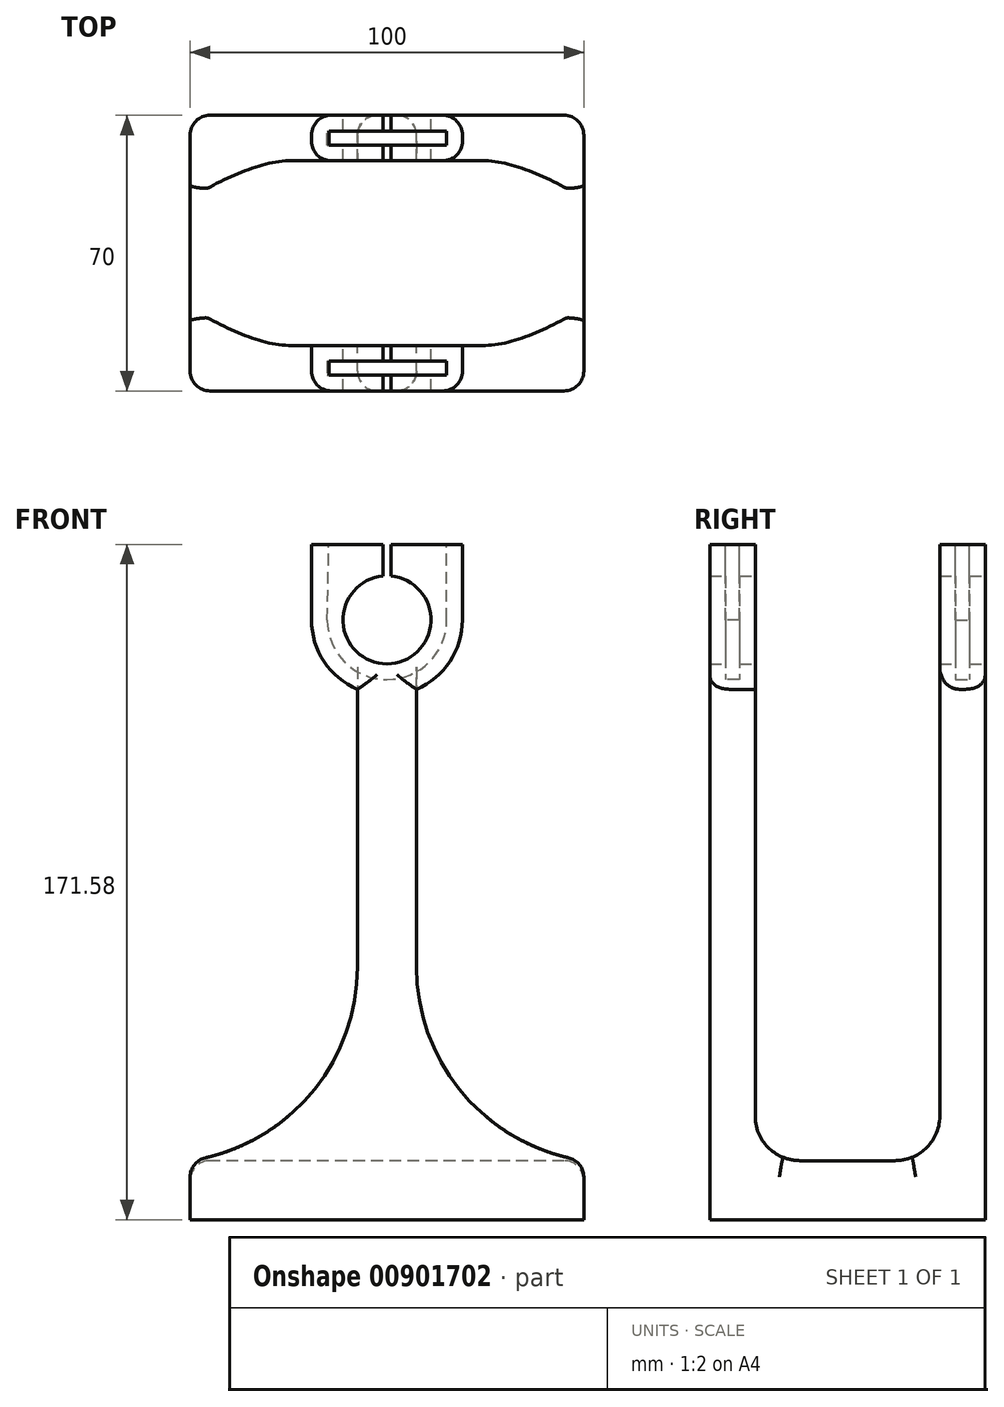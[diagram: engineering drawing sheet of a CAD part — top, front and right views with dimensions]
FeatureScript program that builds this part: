
annotation { "Feature Type Name" : "Feature", "Feature Type Description" : "" }
export const myFeature = defineFeature(function(context is Context, id is Id, definition is map)
    precondition{}
    {
        {
            var Q0;
            Q0=qCreatedBy(makeId("Front.planeOp"),FACE);
            var sketch = newSketch(context, id + "F0", { "sketchPlane" : qUnion([Q0])});
            skPoint(sketch, "E0.middle", {"position": v(0, 0) * mm});
            skArc(sketch, "E1", {"start": v(-15.18, 20.78) * mm, "mid": v(-13.12, 13.15) * mm, "end": v(-7.5, 7.59) * mm});
            skLineSegment(sketch, "E2.top", {"start": v(-19.18, 39.96) * mm, "end": v(19.17, 39.96) * mm});
            skLineSegment(sketch, "E2.left", {"start": v(-19.17, 20.78) * mm, "end": v(-19.17, 39.96) * mm});
            skLineSegment(sketch, "E2.right", {"start": v(19.17, 20.78) * mm, "end": v(19.17, 39.96) * mm});
            skArc(sketch, "E3", {"start": v(-19.17, 20.78) * mm, "mid": v(-16, 10.2) * mm, "end": v(-7.5, 3.13) * mm});
            skLineSegment(sketch, "E4", {"start": v(-15.18, 20.78) * mm, "end": v(-14.78, 39.96) * mm});
            skLineSegment(sketch, "E5", {"start": v(15.18, 20.78) * mm, "end": v(15.18, 39.96) * mm});
            skLineSegment(sketch, "E6.top", {"start": v(-7.5, -131.62) * mm, "end": v(7.5, -131.62) * mm});
            skLineSegment(sketch, "E7.bottom", {"start": v(-50, -131.62) * mm, "end": v(50, -131.62) * mm});
            skLineSegment(sketch, "E7.top", {"start": v(-50, -116.62) * mm, "end": v(-7.5, -116.62) * mm});
            skLineSegment(sketch, "E7.left", {"start": v(-50, -131.62) * mm, "end": v(-50, -116.62) * mm});
            skLineSegment(sketch, "E7.right", {"start": v(50, -131.62) * mm, "end": v(50, -116.62) * mm});
            skLineSegment(sketch, "E8", {"start": v(7.5, -116.62) * mm, "end": v(50, -116.62) * mm});
            skArc(sketch, "E9", {"start": v(7.5, 3.13) * mm, "mid": v(16, 10.2) * mm, "end": v(19.17, 20.78) * mm});
            skLineSegment(sketch, "E10", {"start": v(-7.5, 3.13) * mm, "end": v(-7.5, -116.62) * mm});
            skLineSegment(sketch, "E11", {"start": v(-7.5, 7.59) * mm, "end": v(-7.5, 7.59) * mm});
            skArc(sketch, "E12", {"start": v(7.5, 7.59) * mm, "mid": v(13.12, 13.15) * mm, "end": v(15.18, 20.78) * mm});
            skArc(sketch, "E13", {"start": v(-7.5, 7.59) * mm, "mid": v(0, 5.6) * mm, "end": v(7.5, 7.59) * mm});
            skLineSegment(sketch, "E14", {"start": v(7.5, 3.13) * mm, "end": v(7.5, -116.62) * mm});
            skPoint(sketch, "E15", {"position": v(0, 5.6) * mm});
            skCircle(sketch, "E16", {"center": v(0, 20.78) * mm, "radius": 11.18 * mm});
            skLineSegment(sketch, "E17.bottom", {"start": v(1, 20.78) * mm, "end": v(-1, 20.78) * mm});
            skLineSegment(sketch, "E17.top", {"start": v(1, 39.96) * mm, "end": v(-1, 39.96) * mm});
            skLineSegment(sketch, "E17.left", {"start": v(1, 20.78) * mm, "end": v(1, 39.96) * mm});
            skLineSegment(sketch, "E17.right", {"start": v(-1, 20.78) * mm, "end": v(-1, 39.96) * mm});
            skSolve(sketch);
        }
        {
            var Q0;
            Q0=makeQuery(id+"F0.imprint","IMPRINT",FACE,{"disambiguationData":[TD([[makeQuery(id+"F0.imprint","IMPRINT",EDGE,{"derivedFrom":sQuery(id+"F0.wireOp",EDGE,"E1")}),-1.0]])]});
            var Q1;
            Q1=makeQuery(id+"F0.imprint","IMPRINT",FACE,{"disambiguationData":[TD([[makeQuery(id+"F0.imprint","IMPRINT",EDGE,{"derivedFrom":sQuery(id+"F0.wireOp",EDGE,"E1")}),1.0]])]});
            extrude(context, id + "F1", {"entities" : qUnion([Q0, Q1]), "depth" : 70 * mm, "offsetDistance" : 25 * mm});
        }
        {
            var Q0;
            Q0=makeQuery(id+"F1.opExtrude","SWEPT_FACE",FACE,{"disambiguationData":[OSD([sQuery(id+"F0.wireOp",EDGE,"E2.top")])]});
            var Q1;
            Q1=makeQuery(id+"F1.opExtrude","SWEPT_FACE",FACE,{"disambiguationData":[OSD([sQuery(id+"F0.wireOp",EDGE,"E2.top")])]});
            var sketch = newSketch(context, id + "F2", { "sketchPlane" : qUnion([Q0, Q1])});
            skLineSegment(sketch, "E18.0", {"start": v(19.17, -70) * mm, "end": v(19.17, 0) * mm});
            skLineSegment(sketch, "E19.0", {"start": v(-19.17, -70) * mm, "end": v(-19.17, 0) * mm});
            skLineSegment(sketch, "E20.0", {"start": v(-19.17, -70) * mm, "end": v(19.17, -70) * mm});
            skLineSegment(sketch, "E21.0", {"start": v(-19.18, 0) * mm, "end": v(19.17, 0) * mm});
            skLineSegment(sketch, "E22.bottom", {"start": v(-19.17, -11.55) * mm, "end": v(19.17, -11.55) * mm});
            skLineSegment(sketch, "E22.top", {"start": v(-19.17, -58.45) * mm, "end": v(19.17, -58.45) * mm});
            skLineSegment(sketch, "E22.left", {"start": v(-19.17, -11.55) * mm, "end": v(-19.17, -58.45) * mm});
            skLineSegment(sketch, "E22.right", {"start": v(19.17, -11.55) * mm, "end": v(19.17, -58.45) * mm});
            skLineSegment(sketch, "E23.bottom", {"start": v(15.17, -66) * mm, "end": v(-15.18, -66) * mm});
            skLineSegment(sketch, "E23.top", {"start": v(15.17, -62.45) * mm, "end": v(-15.18, -62.45) * mm});
            skLineSegment(sketch, "E23.left", {"start": v(15.17, -66) * mm, "end": v(15.17, -62.45) * mm});
            skLineSegment(sketch, "E23.right", {"start": v(-15.18, -66) * mm, "end": v(-15.18, -62.45) * mm});
            skLineSegment(sketch, "E24.bottom", {"start": v(15.17, -7.55) * mm, "end": v(-15.18, -7.55) * mm});
            skLineSegment(sketch, "E24.top", {"start": v(15.17, -4) * mm, "end": v(-15.18, -4) * mm});
            skLineSegment(sketch, "E24.left", {"start": v(15.17, -7.55) * mm, "end": v(15.17, -4) * mm});
            skLineSegment(sketch, "E24.right", {"start": v(-15.18, -7.55) * mm, "end": v(-15.18, -4) * mm});
            skSolve(sketch);
        }
        {
            var Q0;
            Q0=makeQuery(id+"F2.imprint","IMPRINT",FACE,{"disambiguationData":[TD([[makeQuery(id+"F2.imprint","IMPRINT",EDGE,{"derivedFrom":sQuery(id+"F2.wireOp",EDGE,"E22.bottom")}),-1.0]])]});
            var Q1;
            Q1=makeQuery(id+"F1.opExtrude","SWEPT_FACE",FACE,{"disambiguationData":[OSD([sQuery(id+"F0.wireOp",EDGE,"E8")])]});
            extrude(context, id + "F3", {"entities" : qUnion([Q0]), "operationType" : NewBodyOperationType.REMOVE, "endBound" : BoundingType.UP_TO_SURFACE, "oppositeDirection" : true, "depth" : 25 * mm, "endBoundEntityFace" : qUnion([Q1]), "offsetDistance" : 25 * mm});
        }
        {
            var Q0;
            Q0=makeQuery(id+"F0.imprint","IMPRINT",FACE,{"disambiguationData":[TD([[makeQuery(id+"F0.imprint","IMPRINT",EDGE,{"derivedFrom":sQuery(id+"F0.wireOp",EDGE,"E1")}),1.0]])]});
            extrude(context, id + "F4", {"entities" : qUnion([Q0]), "operationType" : NewBodyOperationType.REMOVE, "depth" : 7.55 * mm, "hasOffset" : true, "offsetDistance" : (2.75 + .8) * mm, "offsetOppositeDirection" : true, "hasSecondDirection" : true, "secondDirectionOppositeDirection" : false, "secondDirectionDepth" : 4 * mm});
        }
        {
            var Q0;
            Q0=makeQuery(id+"F1.opExtrude","CAP_FACE",FACE,{"disambiguationData":[OSD([sQuery(id+"F0.wireOp",EDGE,"E2.top"),sQuery(id+"F0.wireOp",EDGE,"E2.left"),sQuery(id+"F0.wireOp",EDGE,"E2.right"),sQuery(id+"F0.wireOp",EDGE,"E3"),sQuery(id+"F0.wireOp",EDGE,"E7.bottom"),sQuery(id+"F0.wireOp",EDGE,"E7.top"),sQuery(id+"F0.wireOp",EDGE,"E7.left"),sQuery(id+"F0.wireOp",EDGE,"E7.right"),sQuery(id+"F0.wireOp",EDGE,"E8"),sQuery(id+"F0.wireOp",EDGE,"E9"),sQuery(id+"F0.wireOp",EDGE,"E10"),sQuery(id+"F0.wireOp",EDGE,"E14")])],"isStart":false});
            var sketch = newSketch(context, id + "F5", { "sketchPlane" : qUnion([Q0])});
            skArc(sketch, "E25.0", {"start": v(-15.18, 20.78) * mm, "mid": v(-13.12, 13.15) * mm, "end": v(-7.5, 7.59) * mm});
            skArc(sketch, "E26.0", {"start": v(-7.5, 7.59) * mm, "mid": v(0, 5.6) * mm, "end": v(7.5, 7.59) * mm});
            skArc(sketch, "E27.0", {"start": v(7.5, 7.59) * mm, "mid": v(13.12, 13.15) * mm, "end": v(15.18, 20.78) * mm});
            skLineSegment(sketch, "E28.0", {"start": v(15.18, 20.78) * mm, "end": v(15.18, 39.96) * mm});
            skLineSegment(sketch, "E29.0", {"start": v(-19.18, 39.96) * mm, "end": v(19.17, 39.96) * mm});
            skLineSegment(sketch, "E30.0", {"start": v(-15.18, 20.78) * mm, "end": v(-14.78, 39.96) * mm});
            skSolve(sketch);
        }
        {
            var Q0;
            Q0=makeQuery(id+"F5.imprint","IMPRINT",FACE,{"disambiguationData":[TD([[makeQuery(id+"F5.imprint","IMPRINT",EDGE,{"derivedFrom":sQuery(id+"F5.wireOp",EDGE,"E25.0")}),1.0]])]});
            extrude(context, id + "F6", {"entities" : qUnion([Q0]), "operationType" : NewBodyOperationType.REMOVE, "oppositeDirection" : true, "depth" : 7.55 * mm, "offsetDistance" : 25 * mm, "hasSecondDirection" : true, "secondDirectionOppositeDirection" : true, "secondDirectionDepth" : 4 * mm});
        }
        {
            var Q0;
            {var subQ0=sQuery(id+"F0.wireOp",EDGE,"E14");var subQ1=sQuery(id+"F0.wireOp",EDGE,"E8");var subQ3=sQuery(id+"F2.wireOp",EDGE,"E22.bottom");Q0=makeQuery(id+"F3.boolean.opBoolean","SPLIT",EDGE,{"disambiguationData":[TD([makeQuery(id+"F3.opExtrude","SWEPT_FACE",FACE,{"disambiguationData":[OSD([subQ3])]})])],"derivedFrom":makeQuery(id+"F1.opExtrude","SWEPT_EDGE",EDGE,{"disambiguationData":[OSD([subQ1,subQ0])]})});}
            var Q1;
            {var subQ1=sQuery(id+"F0.wireOp",EDGE,"E10");var subQ2=sQuery(id+"F0.wireOp",EDGE,"E7.top");var subQ3=sQuery(id+"F2.wireOp",EDGE,"E22.bottom");Q1=makeQuery(id+"F3.boolean.opBoolean","SPLIT",EDGE,{"disambiguationData":[TD([makeQuery(id+"F3.opExtrude","SWEPT_FACE",FACE,{"disambiguationData":[OSD([subQ3])]})])],"derivedFrom":makeQuery(id+"F1.opExtrude","SWEPT_EDGE",EDGE,{"disambiguationData":[OSD([subQ2,subQ1])]})});}
            var Q2;
            {var subQ1=sQuery(id+"F0.wireOp",EDGE,"E10");var subQ2=sQuery(id+"F0.wireOp",EDGE,"E7.top");var subQ3=sQuery(id+"F2.wireOp",EDGE,"E22.top");Q2=makeQuery(id+"F3.boolean.opBoolean","SPLIT",EDGE,{"disambiguationData":[TD([makeQuery(id+"F3.opExtrude","SWEPT_FACE",FACE,{"disambiguationData":[OSD([subQ3])]})])],"derivedFrom":makeQuery(id+"F1.opExtrude","SWEPT_EDGE",EDGE,{"disambiguationData":[OSD([subQ2,subQ1])]})});}
            var Q3;
            {var subQ0=sQuery(id+"F0.wireOp",EDGE,"E14");var subQ1=sQuery(id+"F0.wireOp",EDGE,"E8");var subQ3=sQuery(id+"F2.wireOp",EDGE,"E22.top");Q3=makeQuery(id+"F3.boolean.opBoolean","SPLIT",EDGE,{"disambiguationData":[TD([makeQuery(id+"F3.opExtrude","SWEPT_FACE",FACE,{"disambiguationData":[OSD([subQ3])]})])],"derivedFrom":makeQuery(id+"F1.opExtrude","SWEPT_EDGE",EDGE,{"disambiguationData":[OSD([subQ1,subQ0])]})});}
            fillet(context, id + "F7", {"entities" : qUnion([Q0, Q1, Q2, Q3]), "radius" : 49.73 * mm, "tangentPropagation" : true, "allowEdgeOverflow" : false});
        }
        {
            var Q0;
            Q0=makeQuery(id+"F3.boolean.opBoolean","COPY",EDGE,{"derivedFrom":makeQuery(id+"F3.opExtrude","CAP_EDGE",EDGE,{"disambiguationData":[OSD([sQuery(id+"F2.wireOp",EDGE,"E22.top")])],"isStart":false})});
            var Q1;
            Q1=makeQuery(id+"F3.boolean.opBoolean","COPY",EDGE,{"derivedFrom":makeQuery(id+"F3.opExtrude","CAP_EDGE",EDGE,{"disambiguationData":[OSD([sQuery(id+"F2.wireOp",EDGE,"E22.bottom")])],"isStart":false})});
            fillet(context, id + "F8", {"entities" : qUnion([Q0, Q1]), "radius" : 11.35 * mm, "tangentPropagation" : true, "allowEdgeOverflow" : false});
        }
        {
            var Q0;
            Q0=qCreatedBy(makeId("Front.planeOp"),FACE);
            var sketch = newSketch(context, id + "F9", { "sketchPlane" : qUnion([Q0])});
            skLineSegment(sketch, "E31.bottom", {"start": v(69.4, 0) * mm, "end": v(-88.03, 0) * mm});
            skLineSegment(sketch, "E31.top", {"start": v(69.4, -146.73) * mm, "end": v(-88.03, -146.73) * mm});
            skLineSegment(sketch, "E31.left", {"start": v(69.4, 0) * mm, "end": v(69.4, -146.73) * mm});
            skLineSegment(sketch, "E31.right", {"start": v(-88.03, 0) * mm, "end": v(-88.03, -146.73) * mm});
            skSolve(sketch);
        }
        {
            var Q0;
            Q0=makeQuery(id+"F1.opExtrude","SWEPT_EDGE",EDGE,{"disambiguationData":[OSD([sQuery(id+"F0.wireOp",EDGE,"E7.right"),sQuery(id+"F0.wireOp",EDGE,"E8")])]});
            var Q1;
            {var subQ0=sQuery(id+"F0.wireOp",EDGE,"E7.right");var subQ1=sQuery(id+"F0.wireOp",EDGE,"E14");var subQ2=sQuery(id+"F0.wireOp",EDGE,"E8");var subQ4=sQuery(id+"F2.wireOp",EDGE,"E22.bottom");Q1=makeQuery(id+"F7.opFillet","BLEND_EDGE",EDGE,{"blendedFrom":[makeQuery(id+"F3.boolean.opBoolean","SPLIT",EDGE,{"disambiguationData":[TD([makeQuery(id+"F3.opExtrude","SWEPT_FACE",FACE,{"disambiguationData":[OSD([subQ4])]})])],"derivedFrom":makeQuery(id+"F1.opExtrude","SWEPT_EDGE",EDGE,{"disambiguationData":[OSD([subQ2,subQ1])]})}),makeQuery(id+"F1.opExtrude","SWEPT_FACE",FACE,{"disambiguationData":[OSD([subQ0])]})],"blendedInto":[makeQuery(id+"F1.opExtrude","SWEPT_FACE",FACE,{"disambiguationData":[OSD([subQ0])]})]});}
            var Q2;
            {var subQ0=sQuery(id+"F0.wireOp",EDGE,"E7.right");var subQ1=sQuery(id+"F0.wireOp",EDGE,"E14");var subQ2=sQuery(id+"F0.wireOp",EDGE,"E8");var subQ4=sQuery(id+"F2.wireOp",EDGE,"E22.top");Q2=makeQuery(id+"F7.opFillet","BLEND_EDGE",EDGE,{"blendedFrom":[makeQuery(id+"F3.boolean.opBoolean","SPLIT",EDGE,{"disambiguationData":[TD([makeQuery(id+"F3.opExtrude","SWEPT_FACE",FACE,{"disambiguationData":[OSD([subQ4])]})])],"derivedFrom":makeQuery(id+"F1.opExtrude","SWEPT_EDGE",EDGE,{"disambiguationData":[OSD([subQ2,subQ1])]})}),makeQuery(id+"F1.opExtrude","SWEPT_FACE",FACE,{"disambiguationData":[OSD([subQ0])]})],"blendedInto":[makeQuery(id+"F1.opExtrude","SWEPT_FACE",FACE,{"disambiguationData":[OSD([subQ0])]})]});}
            var Q3;
            {var subQ0=sQuery(id+"F0.wireOp",EDGE,"E7.left");var subQ2=sQuery(id+"F0.wireOp",EDGE,"E10");var subQ3=sQuery(id+"F0.wireOp",EDGE,"E7.top");var subQ4=sQuery(id+"F2.wireOp",EDGE,"E22.bottom");Q3=makeQuery(id+"F7.opFillet","BLEND_EDGE",EDGE,{"blendedFrom":[makeQuery(id+"F3.boolean.opBoolean","SPLIT",EDGE,{"disambiguationData":[TD([makeQuery(id+"F3.opExtrude","SWEPT_FACE",FACE,{"disambiguationData":[OSD([subQ4])]})])],"derivedFrom":makeQuery(id+"F1.opExtrude","SWEPT_EDGE",EDGE,{"disambiguationData":[OSD([subQ3,subQ2])]})}),makeQuery(id+"F1.opExtrude","SWEPT_FACE",FACE,{"disambiguationData":[OSD([subQ0])]})],"blendedInto":[makeQuery(id+"F1.opExtrude","SWEPT_FACE",FACE,{"disambiguationData":[OSD([subQ0])]})]});}
            var Q4;
            Q4=makeQuery(id+"F1.opExtrude","SWEPT_EDGE",EDGE,{"disambiguationData":[OSD([sQuery(id+"F0.wireOp",EDGE,"E7.top"),sQuery(id+"F0.wireOp",EDGE,"E7.left")])]});
            var Q5;
            {var subQ0=sQuery(id+"F0.wireOp",EDGE,"E7.left");var subQ2=sQuery(id+"F0.wireOp",EDGE,"E10");var subQ3=sQuery(id+"F0.wireOp",EDGE,"E7.top");var subQ4=sQuery(id+"F2.wireOp",EDGE,"E22.top");Q5=makeQuery(id+"F7.opFillet","BLEND_EDGE",EDGE,{"blendedFrom":[makeQuery(id+"F3.boolean.opBoolean","SPLIT",EDGE,{"disambiguationData":[TD([makeQuery(id+"F3.opExtrude","SWEPT_FACE",FACE,{"disambiguationData":[OSD([subQ4])]})])],"derivedFrom":makeQuery(id+"F1.opExtrude","SWEPT_EDGE",EDGE,{"disambiguationData":[OSD([subQ3,subQ2])]})}),makeQuery(id+"F1.opExtrude","SWEPT_FACE",FACE,{"disambiguationData":[OSD([subQ0])]})],"blendedInto":[makeQuery(id+"F1.opExtrude","SWEPT_FACE",FACE,{"disambiguationData":[OSD([subQ0])]})]});}
            var Q6;
            {var subQ0=sQuery(id+"F0.wireOp",EDGE,"E14");var subQ1=sQuery(id+"F0.wireOp",EDGE,"E8");var subQ2=sQuery(id+"F0.wireOp",EDGE,"E7.top");var subQ3=makeQuery(id+"F1.opExtrude","CAP_FACE",FACE,{"disambiguationData":[OSD([sQuery(id+"F0.wireOp",EDGE,"E2.top"),sQuery(id+"F0.wireOp",EDGE,"E2.left"),sQuery(id+"F0.wireOp",EDGE,"E2.right"),sQuery(id+"F0.wireOp",EDGE,"E3"),sQuery(id+"F0.wireOp",EDGE,"E7.bottom"),subQ2,sQuery(id+"F0.wireOp",EDGE,"E7.left"),sQuery(id+"F0.wireOp",EDGE,"E7.right"),subQ1,sQuery(id+"F0.wireOp",EDGE,"E9"),sQuery(id+"F0.wireOp",EDGE,"E10"),subQ0,sQuery(id+"F0.wireOp",EDGE,"E16")])],"isStart":false});var subQ4=sQuery(id+"F2.wireOp",EDGE,"E22.top");Q6=makeQuery(id+"F7.opFillet","BLEND_EDGE",EDGE,{"blendedFrom":[makeQuery(id+"F3.boolean.opBoolean","SPLIT",EDGE,{"disambiguationData":[TD([makeQuery(id+"F3.opExtrude","SWEPT_FACE",FACE,{"disambiguationData":[OSD([subQ4])]})])],"derivedFrom":makeQuery(id+"F1.opExtrude","SWEPT_EDGE",EDGE,{"disambiguationData":[OSD([subQ1,subQ0])]})}),subQ3],"blendedInto":[subQ3]});}
            var Q7;
            {var subQ0=sQuery(id+"F0.wireOp",EDGE,"E10");var subQ1=sQuery(id+"F0.wireOp",EDGE,"E8");var subQ2=sQuery(id+"F0.wireOp",EDGE,"E7.top");var subQ3=makeQuery(id+"F1.opExtrude","CAP_FACE",FACE,{"disambiguationData":[OSD([sQuery(id+"F0.wireOp",EDGE,"E2.top"),sQuery(id+"F0.wireOp",EDGE,"E2.left"),sQuery(id+"F0.wireOp",EDGE,"E2.right"),sQuery(id+"F0.wireOp",EDGE,"E3"),sQuery(id+"F0.wireOp",EDGE,"E7.bottom"),subQ2,sQuery(id+"F0.wireOp",EDGE,"E7.left"),sQuery(id+"F0.wireOp",EDGE,"E7.right"),subQ1,sQuery(id+"F0.wireOp",EDGE,"E9"),subQ0,sQuery(id+"F0.wireOp",EDGE,"E14"),sQuery(id+"F0.wireOp",EDGE,"E16")])],"isStart":false});var subQ4=sQuery(id+"F2.wireOp",EDGE,"E22.top");Q7=makeQuery(id+"F7.opFillet","BLEND_EDGE",EDGE,{"blendedFrom":[makeQuery(id+"F3.boolean.opBoolean","SPLIT",EDGE,{"disambiguationData":[TD([makeQuery(id+"F3.opExtrude","SWEPT_FACE",FACE,{"disambiguationData":[OSD([subQ4])]})])],"derivedFrom":makeQuery(id+"F1.opExtrude","SWEPT_EDGE",EDGE,{"disambiguationData":[OSD([subQ2,subQ0])]})}),subQ3],"blendedInto":[subQ3]});}
            var Q8;
            {var subQ0=sQuery(id+"F0.wireOp",EDGE,"E10");var subQ1=sQuery(id+"F0.wireOp",EDGE,"E8");var subQ2=sQuery(id+"F0.wireOp",EDGE,"E7.top");var subQ3=makeQuery(id+"F1.opExtrude","CAP_FACE",FACE,{"disambiguationData":[OSD([sQuery(id+"F0.wireOp",EDGE,"E2.top"),sQuery(id+"F0.wireOp",EDGE,"E2.left"),sQuery(id+"F0.wireOp",EDGE,"E2.right"),sQuery(id+"F0.wireOp",EDGE,"E3"),sQuery(id+"F0.wireOp",EDGE,"E7.bottom"),subQ2,sQuery(id+"F0.wireOp",EDGE,"E7.left"),sQuery(id+"F0.wireOp",EDGE,"E7.right"),subQ1,sQuery(id+"F0.wireOp",EDGE,"E9"),subQ0,sQuery(id+"F0.wireOp",EDGE,"E14"),sQuery(id+"F0.wireOp",EDGE,"E16")])],"isStart":true});var subQ4=sQuery(id+"F2.wireOp",EDGE,"E22.bottom");Q8=makeQuery(id+"F7.opFillet","BLEND_EDGE",EDGE,{"blendedFrom":[makeQuery(id+"F3.boolean.opBoolean","SPLIT",EDGE,{"disambiguationData":[TD([makeQuery(id+"F3.opExtrude","SWEPT_FACE",FACE,{"disambiguationData":[OSD([subQ4])]})])],"derivedFrom":makeQuery(id+"F1.opExtrude","SWEPT_EDGE",EDGE,{"disambiguationData":[OSD([subQ2,subQ0])]})}),subQ3],"blendedInto":[subQ3]});}
            var Q9;
            {var subQ0=sQuery(id+"F0.wireOp",EDGE,"E14");var subQ1=sQuery(id+"F0.wireOp",EDGE,"E8");var subQ2=sQuery(id+"F0.wireOp",EDGE,"E7.top");var subQ3=makeQuery(id+"F1.opExtrude","CAP_FACE",FACE,{"disambiguationData":[OSD([sQuery(id+"F0.wireOp",EDGE,"E2.top"),sQuery(id+"F0.wireOp",EDGE,"E2.left"),sQuery(id+"F0.wireOp",EDGE,"E2.right"),sQuery(id+"F0.wireOp",EDGE,"E3"),sQuery(id+"F0.wireOp",EDGE,"E7.bottom"),subQ2,sQuery(id+"F0.wireOp",EDGE,"E7.left"),sQuery(id+"F0.wireOp",EDGE,"E7.right"),subQ1,sQuery(id+"F0.wireOp",EDGE,"E9"),sQuery(id+"F0.wireOp",EDGE,"E10"),subQ0,sQuery(id+"F0.wireOp",EDGE,"E16")])],"isStart":true});var subQ4=sQuery(id+"F2.wireOp",EDGE,"E22.bottom");Q9=makeQuery(id+"F7.opFillet","BLEND_EDGE",EDGE,{"blendedFrom":[makeQuery(id+"F3.boolean.opBoolean","SPLIT",EDGE,{"disambiguationData":[TD([makeQuery(id+"F3.opExtrude","SWEPT_FACE",FACE,{"disambiguationData":[OSD([subQ4])]})])],"derivedFrom":makeQuery(id+"F1.opExtrude","SWEPT_EDGE",EDGE,{"disambiguationData":[OSD([subQ1,subQ0])]})}),subQ3],"blendedInto":[subQ3]});}
            var Q10;
            Q10=makeQuery(id+"F1.opExtrude","CAP_EDGE",EDGE,{"disambiguationData":[OSD([sQuery(id+"F0.wireOp",EDGE,"E2.left")])],"isStart":true});
            var Q11;
            Q11=makeQuery(id+"F3.boolean.opBoolean","COPY",EDGE,{"derivedFrom":makeQuery(id+"F3.opExtrude","SWEPT_EDGE",EDGE,{"disambiguationData":[OSD([sQuery(id+"F2.wireOp",EDGE,"E19.0"),sQuery(id+"F2.wireOp",EDGE,"E22.bottom"),sQuery(id+"F2.wireOp",EDGE,"E22.left")])]})});
            var Q12;
            Q12=makeQuery(id+"F3.boolean.opBoolean","COPY",EDGE,{"derivedFrom":makeQuery(id+"F3.opExtrude","SWEPT_EDGE",EDGE,{"disambiguationData":[OSD([sQuery(id+"F2.wireOp",EDGE,"E18.0"),sQuery(id+"F2.wireOp",EDGE,"E22.bottom"),sQuery(id+"F2.wireOp",EDGE,"E22.right")])]})});
            var Q13;
            Q13=makeQuery(id+"F1.opExtrude","CAP_EDGE",EDGE,{"disambiguationData":[OSD([sQuery(id+"F0.wireOp",EDGE,"E2.right")])],"isStart":true});
            var Q14;
            Q14=makeQuery(id+"F3.boolean.opBoolean","COPY",EDGE,{"derivedFrom":makeQuery(id+"F3.opExtrude","SWEPT_EDGE",EDGE,{"disambiguationData":[OSD([sQuery(id+"F2.wireOp",EDGE,"E18.0"),sQuery(id+"F2.wireOp",EDGE,"E22.top"),sQuery(id+"F2.wireOp",EDGE,"E22.right")])]})});
            var Q15;
            Q15=makeQuery(id+"F1.opExtrude","CAP_EDGE",EDGE,{"disambiguationData":[OSD([sQuery(id+"F0.wireOp",EDGE,"E2.right")])],"isStart":false});
            var Q16;
            Q16=makeQuery(id+"F1.opExtrude","CAP_EDGE",EDGE,{"disambiguationData":[OSD([sQuery(id+"F0.wireOp",EDGE,"E2.left")])],"isStart":false});
            var Q17;
            Q17=makeQuery(id+"F3.boolean.opBoolean","COPY",EDGE,{"derivedFrom":makeQuery(id+"F3.opExtrude","SWEPT_EDGE",EDGE,{"disambiguationData":[OSD([sQuery(id+"F2.wireOp",EDGE,"E19.0"),sQuery(id+"F2.wireOp",EDGE,"E22.top"),sQuery(id+"F2.wireOp",EDGE,"E22.left")])]})});
            var Q18;
            Q18=makeQuery(id+"F1.opExtrude","CAP_EDGE",EDGE,{"disambiguationData":[OSD([sQuery(id+"F0.wireOp",EDGE,"E7.right")])],"isStart":false});
            var Q19;
            Q19=makeQuery(id+"F1.opExtrude","CAP_EDGE",EDGE,{"disambiguationData":[OSD([sQuery(id+"F0.wireOp",EDGE,"E7.right")])],"isStart":true});
            var Q20;
            Q20=makeQuery(id+"F1.opExtrude","CAP_EDGE",EDGE,{"disambiguationData":[OSD([sQuery(id+"F0.wireOp",EDGE,"E7.left")])],"isStart":true});
            var Q21;
            Q21=makeQuery(id+"F1.opExtrude","CAP_EDGE",EDGE,{"disambiguationData":[OSD([sQuery(id+"F0.wireOp",EDGE,"E7.left")])],"isStart":false});
            fillet(context, id + "F10", {"entities" : qUnion([Q0, Q1, Q2, Q3, Q4, Q5, Q6, Q7, Q8, Q9, Q10, Q11, Q12, Q13, Q14, Q15, Q16, Q17, Q18, Q19, Q20, Q21]), "radius" : 5 * mm, "tangentPropagation" : true, "allowEdgeOverflow" : false});
        }
    });
